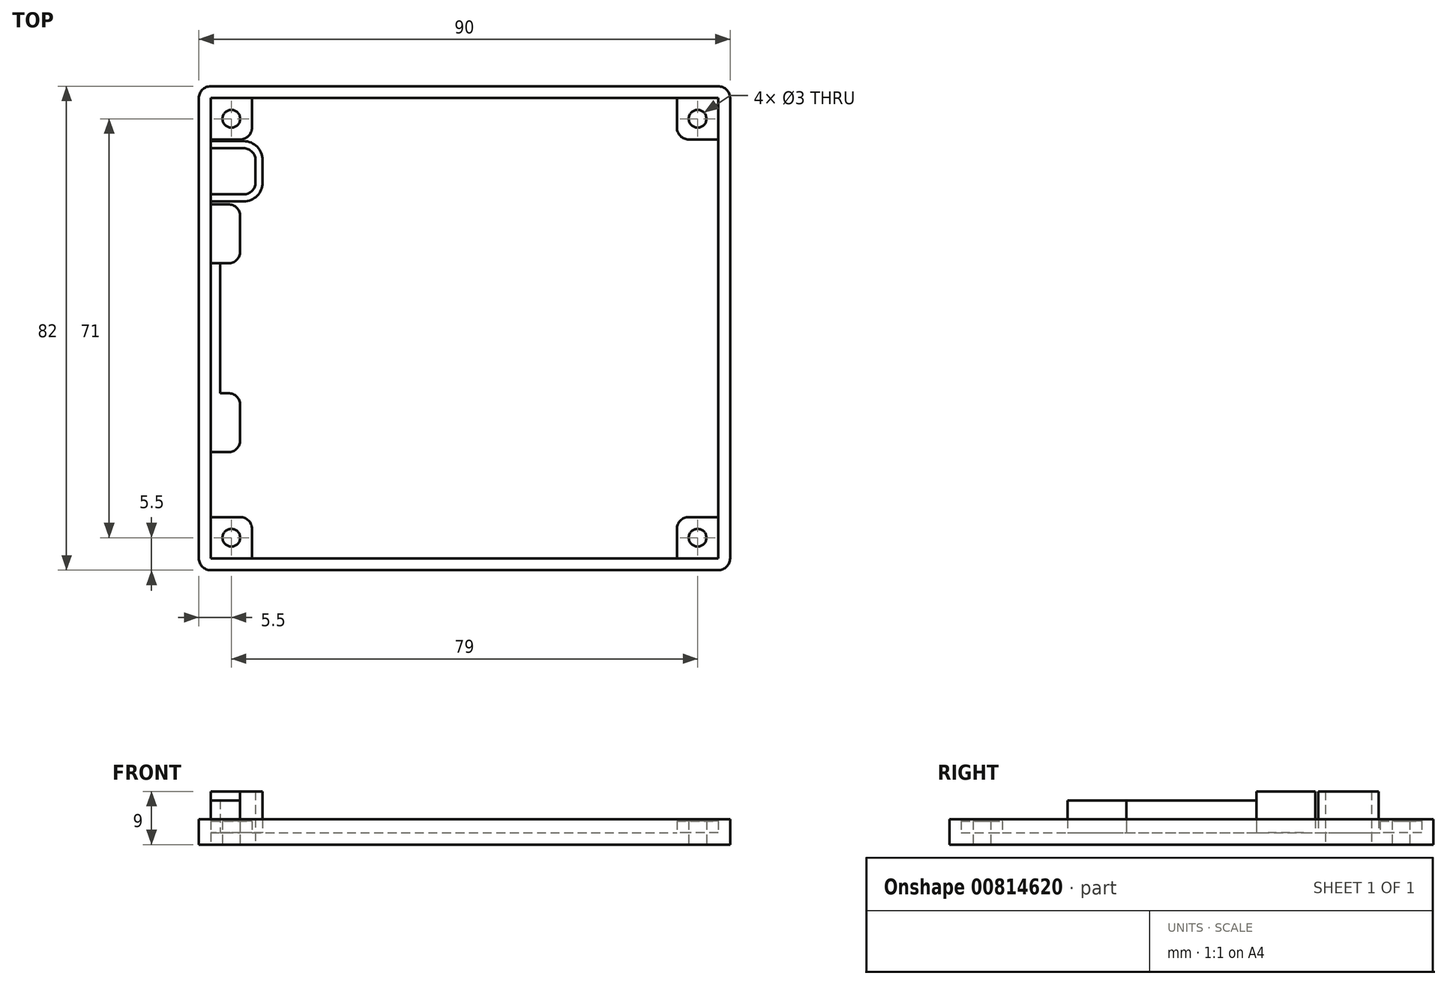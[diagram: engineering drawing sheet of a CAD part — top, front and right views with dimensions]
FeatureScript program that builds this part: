
annotation { "Feature Type Name" : "Feature", "Feature Type Description" : "" }
export const myFeature = defineFeature(function(context is Context, id is Id, definition is map)
    precondition{}
    {
        {
            var Q0;
            Q0=qCreatedBy(makeId("Top.planeOp"),FACE);
            var sketch = newSketch(context, id + "F0", { "sketchPlane" : qUnion([Q0])});
            skLineSegment(sketch, "E0.bottom", {"start": v(2, 0) * mm, "end": v(88, 0) * mm});
            skLineSegment(sketch, "E0.top", {"start": v(2, 82) * mm, "end": v(88, 82) * mm});
            skLineSegment(sketch, "E0.left", {"start": v(0, 2) * mm, "end": v(0, 80) * mm});
            skLineSegment(sketch, "E0.right", {"start": v(90, 2) * mm, "end": v(90, 80) * mm});
            skPoint(sketch, "E1.visualSharp", {"position": v(0, 82) * mm});
            skArc(sketch, "E1.filletArc", {"start": v(2, 82) * mm, "mid": v(0.59, 81.41) * mm, "end": v(0, 80) * mm});
            skPoint(sketch, "E2.visualSharp", {"position": v(0, 0) * mm});
            skArc(sketch, "E2.filletArc", {"start": v(0, 2) * mm, "mid": v(0.59, 0.59) * mm, "end": v(2, 0) * mm});
            skPoint(sketch, "E3.visualSharp", {"position": v(90, 0) * mm});
            skArc(sketch, "E3.filletArc", {"start": v(88, 0) * mm, "mid": v(89.41, 0.59) * mm, "end": v(90, 2) * mm});
            skPoint(sketch, "E4.visualSharp", {"position": v(90, 82) * mm});
            skArc(sketch, "E4.filletArc", {"start": v(90, 80) * mm, "mid": v(89.41, 81.41) * mm, "end": v(88, 82) * mm});
            skSolve(sketch);
        }
        {
            var Q0;
            Q0=makeQuery(id+"F0.imprint","IMPRINT",FACE,{"disambiguationData":[TD([[makeQuery(id+"F0.imprint","IMPRINT",EDGE,{"derivedFrom":sQuery(id+"F0.wireOp",EDGE,"E0.bottom")}),1.0]])]});
            extrude(context, id + "F1", {"entities" : qUnion([Q0]), "depth" : 2 * mm, "offsetDistance" : 25 * mm});
        }
        {
            var Q0;
            Q0=makeQuery(id+"F1.opExtrude","CAP_FACE",FACE,{"disambiguationData":[OSD([sQuery(id+"F0.wireOp",EDGE,"E0.bottom"),sQuery(id+"F0.wireOp",EDGE,"E0.top"),sQuery(id+"F0.wireOp",EDGE,"E0.left"),sQuery(id+"F0.wireOp",EDGE,"E0.right"),sQuery(id+"F0.wireOp",EDGE,"E1.filletArc"),sQuery(id+"F0.wireOp",EDGE,"E2.filletArc"),sQuery(id+"F0.wireOp",EDGE,"E3.filletArc"),sQuery(id+"F0.wireOp",EDGE,"E4.filletArc")])],"isStart":false});
            var sketch = newSketch(context, id + "F2", { "sketchPlane" : qUnion([Q0])});
            skLineSegment(sketch, "E5.0", {"start": v(2, 80) * mm, "end": v(88, 80) * mm});
            skLineSegment(sketch, "E5.2", {"start": v(2, 80) * mm, "end": v(2, 80) * mm});
            skLineSegment(sketch, "E5.3", {"start": v(88, 2) * mm, "end": v(88, 80) * mm});
            skLineSegment(sketch, "E5.4", {"start": v(2, 2) * mm, "end": v(2, 80) * mm});
            skLineSegment(sketch, "E5.5", {"start": v(2, 2) * mm, "end": v(2, 2) * mm});
            skLineSegment(sketch, "E5.6", {"start": v(2, 2) * mm, "end": v(88, 2) * mm});
            skSolve(sketch);
        }
        {
            var Q0;
            Q0=makeQuery(id+"F2.imprint","IMPRINT",FACE,{"disambiguationData":[TD([[makeQuery(id+"F2.imprint","IMPRINT",EDGE,{"derivedFrom":sQuery(id+"F2.wireOp",EDGE,"E5.0")}),1.0]])]});
            extrude(context, id + "F3", {"entities" : qUnion([Q0]), "operationType" : NewBodyOperationType.ADD, "depth" : 2.3 * mm, "offsetDistance" : 25 * mm});
        }
        {
            var Q0;
            Q0=makeQuery(id+"F1.opExtrude","CAP_FACE",FACE,{"disambiguationData":[OSD([sQuery(id+"F0.wireOp",EDGE,"E0.bottom"),sQuery(id+"F0.wireOp",EDGE,"E0.top"),sQuery(id+"F0.wireOp",EDGE,"E0.left"),sQuery(id+"F0.wireOp",EDGE,"E0.right"),sQuery(id+"F0.wireOp",EDGE,"E1.filletArc"),sQuery(id+"F0.wireOp",EDGE,"E2.filletArc"),sQuery(id+"F0.wireOp",EDGE,"E3.filletArc"),sQuery(id+"F0.wireOp",EDGE,"E4.filletArc")])],"isStart":false});
            var sketch = newSketch(context, id + "F4", { "sketchPlane" : qUnion([Q0])});
            skLineSegment(sketch, "E6.bottom", {"start": v(2, 2) * mm, "end": v(9, 2) * mm});
            skLineSegment(sketch, "E6.top", {"start": v(2, 9) * mm, "end": v(7, 9) * mm});
            skLineSegment(sketch, "E6.left", {"start": v(2, 2) * mm, "end": v(2, 9) * mm});
            skLineSegment(sketch, "E6.right", {"start": v(9, 2) * mm, "end": v(9, 7) * mm});
            skLineSegment(sketch, "E7.bottom", {"start": v(2, 80) * mm, "end": v(9, 80) * mm});
            skLineSegment(sketch, "E7.top", {"start": v(2, 73) * mm, "end": v(7, 73) * mm});
            skLineSegment(sketch, "E7.left", {"start": v(2, 80) * mm, "end": v(2, 73) * mm});
            skLineSegment(sketch, "E7.right", {"start": v(9, 80) * mm, "end": v(9, 75) * mm});
            skLineSegment(sketch, "E8.bottom", {"start": v(88, 2) * mm, "end": v(81, 2) * mm});
            skLineSegment(sketch, "E8.top", {"start": v(88, 9) * mm, "end": v(83, 9) * mm});
            skLineSegment(sketch, "E8.left", {"start": v(88, 2) * mm, "end": v(88, 9) * mm});
            skLineSegment(sketch, "E8.right", {"start": v(81, 2) * mm, "end": v(81, 7) * mm});
            skLineSegment(sketch, "E9.bottom", {"start": v(88, 80) * mm, "end": v(81, 80) * mm});
            skLineSegment(sketch, "E9.top", {"start": v(88, 73) * mm, "end": v(83, 73) * mm});
            skLineSegment(sketch, "E9.left", {"start": v(88, 80) * mm, "end": v(88, 73) * mm});
            skLineSegment(sketch, "E9.right", {"start": v(81, 80) * mm, "end": v(81, 75) * mm});
            skPoint(sketch, "E10.visualSharp", {"position": v(9, 9) * mm});
            skArc(sketch, "E10.filletArc", {"start": v(9, 7) * mm, "mid": v(8.41, 8.41) * mm, "end": v(7, 9) * mm});
            skPoint(sketch, "E11.visualSharp", {"position": v(9, 73) * mm});
            skArc(sketch, "E11.filletArc", {"start": v(7, 73) * mm, "mid": v(8.41, 73.59) * mm, "end": v(9, 75) * mm});
            skPoint(sketch, "E12.visualSharp", {"position": v(81, 73) * mm});
            skArc(sketch, "E12.filletArc", {"start": v(81, 75) * mm, "mid": v(81.59, 73.59) * mm, "end": v(83, 73) * mm});
            skPoint(sketch, "E13.visualSharp", {"position": v(81, 9) * mm});
            skArc(sketch, "E13.filletArc", {"start": v(83, 9) * mm, "mid": v(81.59, 8.41) * mm, "end": v(81, 7) * mm});
            skSolve(sketch);
        }
        {
            var Q0;
            Q0=qSketchRegion(id+"F4",true);
            extrude(context, id + "F5", {"entities" : qUnion([Q0]), "operationType" : NewBodyOperationType.ADD, "depth" : 2 * mm, "offsetDistance" : 25 * mm});
        }
        {
            var Q0;
            Q0=makeQuery(id+"F1.opExtrude","CAP_FACE",FACE,{"disambiguationData":[OSD([sQuery(id+"F0.wireOp",EDGE,"E0.bottom"),sQuery(id+"F0.wireOp",EDGE,"E0.top"),sQuery(id+"F0.wireOp",EDGE,"E0.left"),sQuery(id+"F0.wireOp",EDGE,"E0.right"),sQuery(id+"F0.wireOp",EDGE,"E1.filletArc"),sQuery(id+"F0.wireOp",EDGE,"E2.filletArc"),sQuery(id+"F0.wireOp",EDGE,"E3.filletArc"),sQuery(id+"F0.wireOp",EDGE,"E4.filletArc")])],"isStart":true});
            var sketch = newSketch(context, id + "F6", { "sketchPlane" : qUnion([Q0])});
            skCircle(sketch, "E14", {"center": v(84.5, -5.5) * mm, "radius": 1.5 * mm});
            skCircle(sketch, "E15", {"center": v(84.5, -76.5) * mm, "radius": 1.5 * mm});
            skCircle(sketch, "E16", {"center": v(5.5, -76.5) * mm, "radius": 1.5 * mm});
            skCircle(sketch, "E17", {"center": v(5.5, -5.5) * mm, "radius": 1.5 * mm});
            skSolve(sketch);
        }
        {
            var Q0;
            Q0=qSketchRegion(id+"F6",true);
            extrude(context, id + "F7", {"entities" : qUnion([Q0]), "operationType" : NewBodyOperationType.REMOVE, "oppositeDirection" : true, "depth" : 6 * mm, "offsetDistance" : 25 * mm});
        }
        {
            var Q0;
            Q0=makeQuery(id+"F1.opExtrude","CAP_FACE",FACE,{"disambiguationData":[OSD([sQuery(id+"F0.wireOp",EDGE,"E0.bottom"),sQuery(id+"F0.wireOp",EDGE,"E0.top"),sQuery(id+"F0.wireOp",EDGE,"E0.left"),sQuery(id+"F0.wireOp",EDGE,"E0.right"),sQuery(id+"F0.wireOp",EDGE,"E1.filletArc"),sQuery(id+"F0.wireOp",EDGE,"E2.filletArc"),sQuery(id+"F0.wireOp",EDGE,"E3.filletArc"),sQuery(id+"F0.wireOp",EDGE,"E4.filletArc")])],"isStart":false});
            var sketch = newSketch(context, id + "F8", { "sketchPlane" : qUnion([Q0])});
            skLineSegment(sketch, "E18.bottom", {"start": v(2, 62) * mm, "end": v(5, 62) * mm});
            skLineSegment(sketch, "E18.top", {"start": v(2, 52) * mm, "end": v(5, 52) * mm});
            skLineSegment(sketch, "E18.left", {"start": v(2, 62) * mm, "end": v(2, 52) * mm});
            skLineSegment(sketch, "E18.right", {"start": v(7, 60) * mm, "end": v(7, 54) * mm});
            skPoint(sketch, "E19.visualSharp", {"position": v(7, 62) * mm});
            skArc(sketch, "E19.filletArc", {"start": v(7, 60) * mm, "mid": v(6.41, 61.41) * mm, "end": v(5, 62) * mm});
            skPoint(sketch, "E20.visualSharp", {"position": v(7, 52) * mm});
            skArc(sketch, "E20.filletArc", {"start": v(5, 52) * mm, "mid": v(6.41, 52.59) * mm, "end": v(7, 54) * mm});
            skSolve(sketch);
        }
        {
            var Q0;
            Q0=qSketchRegion(id+"F8",true);
            extrude(context, id + "F9", {"entities" : qUnion([Q0]), "operationType" : NewBodyOperationType.ADD, "depth" : 7 * mm, "offsetDistance" : 25 * mm});
        }
        {
            var Q0;
            Q0=makeQuery(id+"F1.opExtrude","CAP_FACE",FACE,{"disambiguationData":[OSD([sQuery(id+"F0.wireOp",EDGE,"E0.bottom"),sQuery(id+"F0.wireOp",EDGE,"E0.top"),sQuery(id+"F0.wireOp",EDGE,"E0.left"),sQuery(id+"F0.wireOp",EDGE,"E0.right"),sQuery(id+"F0.wireOp",EDGE,"E1.filletArc"),sQuery(id+"F0.wireOp",EDGE,"E2.filletArc"),sQuery(id+"F0.wireOp",EDGE,"E3.filletArc"),sQuery(id+"F0.wireOp",EDGE,"E4.filletArc")])],"isStart":false});
            var sketch = newSketch(context, id + "F10", { "sketchPlane" : qUnion([Q0])});
            skLineSegment(sketch, "E21.bottom", {"start": v(2, 20) * mm, "end": v(5, 20) * mm});
            skLineSegment(sketch, "E21.top", {"start": v(2, 30) * mm, "end": v(5, 30) * mm});
            skLineSegment(sketch, "E21.left", {"start": v(2, 20) * mm, "end": v(2, 30) * mm});
            skLineSegment(sketch, "E21.right", {"start": v(7, 22) * mm, "end": v(7, 28) * mm});
            skPoint(sketch, "E22.visualSharp", {"position": v(7, 30) * mm});
            skArc(sketch, "E22.filletArc", {"start": v(7, 28) * mm, "mid": v(6.41, 29.41) * mm, "end": v(5, 30) * mm});
            skPoint(sketch, "E23.visualSharp", {"position": v(7, 20) * mm});
            skArc(sketch, "E23.filletArc", {"start": v(5, 20) * mm, "mid": v(6.41, 20.59) * mm, "end": v(7, 22) * mm});
            skSolve(sketch);
        }
        {
            var Q0;
            Q0=makeQuery(id+"F10.imprint","IMPRINT",FACE,{"disambiguationData":[TD([[makeQuery(id+"F10.imprint","IMPRINT",EDGE,{"derivedFrom":sQuery(id+"F10.wireOp",EDGE,"E21.bottom")}),1.0]])]});
            extrude(context, id + "F11", {"entities" : qUnion([Q0]), "operationType" : NewBodyOperationType.ADD, "depth" : 5.5 * mm, "offsetDistance" : 25 * mm});
        }
        {
            var Q0;
            Q0=makeQuery(id+"F1.opExtrude","CAP_FACE",FACE,{"disambiguationData":[OSD([sQuery(id+"F0.wireOp",EDGE,"E0.bottom"),sQuery(id+"F0.wireOp",EDGE,"E0.top"),sQuery(id+"F0.wireOp",EDGE,"E0.left"),sQuery(id+"F0.wireOp",EDGE,"E0.right"),sQuery(id+"F0.wireOp",EDGE,"E1.filletArc"),sQuery(id+"F0.wireOp",EDGE,"E2.filletArc"),sQuery(id+"F0.wireOp",EDGE,"E3.filletArc"),sQuery(id+"F0.wireOp",EDGE,"E4.filletArc")])],"isStart":true});
            var sketch = newSketch(context, id + "F12", { "sketchPlane" : qUnion([Q0])});
            skLineSegment(sketch, "E24.bottom", {"start": v(2, -71.5) * mm, "end": v(7.6, -71.5) * mm});
            skLineSegment(sketch, "E24.top", {"start": v(2, -63.7) * mm, "end": v(7.6, -63.7) * mm});
            skLineSegment(sketch, "E24.left", {"start": v(2, -71.5) * mm, "end": v(2, -63.7) * mm});
            skLineSegment(sketch, "E24.right", {"start": v(9.6, -69.5) * mm, "end": v(9.6, -65.7) * mm});
            skPoint(sketch, "E25.visualSharp", {"position": v(9.6, -71.5) * mm});
            skArc(sketch, "E25.filletArc", {"start": v(7.6, -71.5) * mm, "mid": v(9.01, -70.91) * mm, "end": v(9.6, -69.5) * mm});
            skPoint(sketch, "E26.visualSharp", {"position": v(9.6, -63.7) * mm});
            skArc(sketch, "E26.filletArc", {"start": v(9.6, -65.7) * mm, "mid": v(9.01, -64.29) * mm, "end": v(7.6, -63.7) * mm});
            skSolve(sketch);
        }
        {
            var Q0;
            Q0=makeQuery(id+"F12.imprint","IMPRINT",FACE,{"disambiguationData":[TD([[makeQuery(id+"F12.imprint","IMPRINT",EDGE,{"derivedFrom":sQuery(id+"F12.wireOp",EDGE,"E24.bottom")}),1.0]])]});
            extrude(context, id + "F13", {"entities" : qUnion([Q0]), "operationType" : NewBodyOperationType.REMOVE, "oppositeDirection" : true, "depth" : 25 * mm, "offsetDistance" : 25 * mm});
        }
        {
            var Q0;
            Q0=makeQuery(id+"F1.opExtrude","CAP_FACE",FACE,{"disambiguationData":[OSD([sQuery(id+"F0.wireOp",EDGE,"E0.bottom"),sQuery(id+"F0.wireOp",EDGE,"E0.top"),sQuery(id+"F0.wireOp",EDGE,"E0.left"),sQuery(id+"F0.wireOp",EDGE,"E0.right"),sQuery(id+"F0.wireOp",EDGE,"E1.filletArc"),sQuery(id+"F0.wireOp",EDGE,"E2.filletArc"),sQuery(id+"F0.wireOp",EDGE,"E3.filletArc"),sQuery(id+"F0.wireOp",EDGE,"E4.filletArc")])],"isStart":false});
            var sketch = newSketch(context, id + "F14", { "sketchPlane" : qUnion([Q0])});
            skLineSegment(sketch, "E27.0", {"start": v(7.6, 72.7) * mm, "end": v(2, 72.7) * mm});
            skLineSegment(sketch, "E27.1", {"start": v(7.6, 62.5) * mm, "end": v(2, 62.5) * mm});
            skArc(sketch, "E27.2", {"start": v(7.6, 62.5) * mm, "mid": v(9.86, 63.44) * mm, "end": v(10.8, 65.7) * mm});
            skLineSegment(sketch, "E27.3", {"start": v(10.8, 65.7) * mm, "end": v(10.8, 69.5) * mm});
            skArc(sketch, "E27.4", {"start": v(10.8, 69.5) * mm, "mid": v(9.86, 71.76) * mm, "end": v(7.6, 72.7) * mm});
            skLineSegment(sketch, "E28.0", {"start": v(7.6, 71.5) * mm, "end": v(2, 71.5) * mm});
            skLineSegment(sketch, "E28.1", {"start": v(7.6, 63.7) * mm, "end": v(2, 63.7) * mm});
            skArc(sketch, "E28.2", {"start": v(7.6, 63.7) * mm, "mid": v(9.01, 64.29) * mm, "end": v(9.6, 65.7) * mm});
            skLineSegment(sketch, "E28.3", {"start": v(9.6, 65.7) * mm, "end": v(9.6, 69.5) * mm});
            skArc(sketch, "E28.4", {"start": v(9.6, 69.5) * mm, "mid": v(9.01, 70.91) * mm, "end": v(7.6, 71.5) * mm});
            skLineSegment(sketch, "E29", {"start": v(2, 72.7) * mm, "end": v(2, 71.5) * mm});
            skLineSegment(sketch, "E30", {"start": v(2, 63.7) * mm, "end": v(2, 62.5) * mm});
            skSolve(sketch);
        }
        {
            var Q0;
            Q0=qSketchRegion(id+"F14",true);
            extrude(context, id + "F15", {"entities" : qUnion([Q0]), "operationType" : NewBodyOperationType.ADD, "depth" : 7 * mm, "offsetDistance" : 25 * mm});
        }
        {
            var Q0;
            Q0=makeQuery(id+"F1.opExtrude","CAP_FACE",FACE,{"disambiguationData":[OSD([sQuery(id+"F0.wireOp",EDGE,"E0.bottom"),sQuery(id+"F0.wireOp",EDGE,"E0.top"),sQuery(id+"F0.wireOp",EDGE,"E0.left"),sQuery(id+"F0.wireOp",EDGE,"E0.right"),sQuery(id+"F0.wireOp",EDGE,"E1.filletArc"),sQuery(id+"F0.wireOp",EDGE,"E2.filletArc"),sQuery(id+"F0.wireOp",EDGE,"E3.filletArc"),sQuery(id+"F0.wireOp",EDGE,"E4.filletArc")])],"isStart":false});
            var sketch = newSketch(context, id + "F16", { "sketchPlane" : qUnion([Q0])});
            skLineSegment(sketch, "E31.bottom", {"start": v(2, 30) * mm, "end": v(3.6, 30) * mm});
            skLineSegment(sketch, "E31.top", {"start": v(2, 52) * mm, "end": v(3.6, 52) * mm});
            skLineSegment(sketch, "E31.left", {"start": v(2, 30) * mm, "end": v(2, 52) * mm});
            skLineSegment(sketch, "E31.right", {"start": v(3.6, 30) * mm, "end": v(3.6, 52) * mm});
            skSolve(sketch);
        }
        {
            var Q0;
            Q0=makeQuery(id+"F16.imprint","IMPRINT",FACE,{"disambiguationData":[TD([[makeQuery(id+"F16.imprint","IMPRINT",EDGE,{"derivedFrom":sQuery(id+"F16.wireOp",EDGE,"E31.bottom")}),1.0]])]});
            extrude(context, id + "F17", {"entities" : qUnion([Q0]), "operationType" : NewBodyOperationType.ADD, "depth" : 5.5 * mm, "offsetDistance" : 25 * mm});
        }
    });
